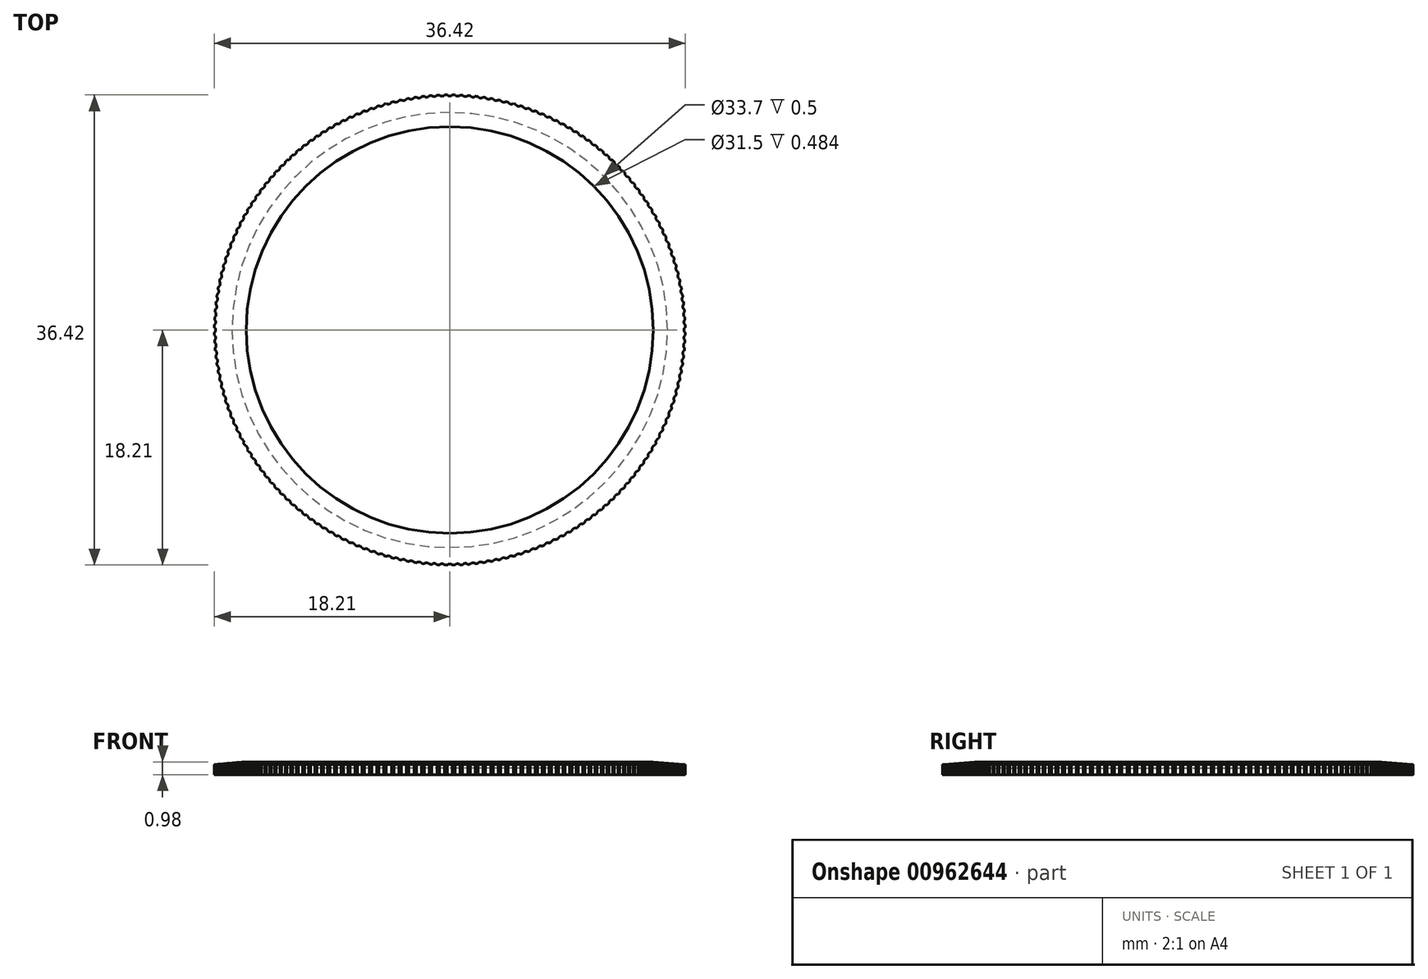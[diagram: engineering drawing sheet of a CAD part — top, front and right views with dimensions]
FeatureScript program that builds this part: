
annotation { "Feature Type Name" : "Feature", "Feature Type Description" : "" }
export const myFeature = defineFeature(function(context is Context, id is Id, definition is map)
    precondition{}
    {
        {
            assignVariable(context, id + "F0", {"name" : "dOut", "anyValue" : 36.43 * mm});
        }
        {
            assignVariable(context, id + "F1", {"name" : "dIn", "anyValue" : 31.5 * mm});
        }
        {
            assignVariable(context, id + "F2", {"name" : "bevelAngle", "anyValue" : 5 * degree});
        }
        {
            var Q0;
            Q0=qCreatedBy(makeId("Top.planeOp"),FACE);
            var sketch = newSketch(context, id + "F3", { "sketchPlane" : qUnion([Q0])});
            skCircle(sketch, "E0", {"center": v(0, 0) * mm, "radius": 18.21 * mm});
            skCircle(sketch, "E1", {"center": v(0, 0) * mm, "radius": 16.85 * mm});
            skCircle(sketch, "E2", {"center": v(0, 0) * mm, "radius": 15.75 * mm});
            skSolve(sketch);
        }
        {
            assignVariable(context, id + "F4", {"name" : "thickness", "anyValue" : 1.2 * mm});
        }
        {
            assignVariable(context, id + "F5", {"name" : "thickness_inside", "anyValue" : 0.7 * mm});
        }
        {
            var Q0;
            Q0=makeQuery(id+"F3.imprint","IMPRINT",FACE,{"disambiguationData":[TD([[makeQuery(id+"F3.imprint","IMPRINT",EDGE,{"derivedFrom":sQuery(id+"F3.wireOp",EDGE,"E0")}),1.0]])]});
            extrude(context, id + "F6", {"entities" : qUnion([Q0]), "oppositeDirection" : true, "depth" : getVariable(context, 'thickness'), "offsetDistance" : 25 * mm});
        }
        {
            var Q0;
            Q0=makeQuery(id+"F3.imprint","IMPRINT",FACE,{"disambiguationData":[TD([[makeQuery(id+"F3.imprint","IMPRINT",EDGE,{"derivedFrom":sQuery(id+"F3.wireOp",EDGE,"E1")}),1.0]])]});
            extrude(context, id + "F7", {"entities" : qUnion([Q0]), "operationType" : NewBodyOperationType.ADD, "oppositeDirection" : true, "depth" : getVariable(context, 'thickness_inside'), "offsetDistance" : 25 * mm});
        }
        {
            var Q0;
            Q0=makeQuery(id+"F6.opExtrude","CAP_EDGE",EDGE,{"disambiguationData":[OSD([sQuery(id+"F3.wireOp",EDGE,"E0")])],"isStart":true});
            chamfer(context, id + "F8", {"entities" : qUnion([Q0]), "chamferType" : ChamferType.OFFSET_ANGLE, "width" : getVariable(context, 'dOut') - getVariable(context, 'dIn'), "oppositeDirection" : false, "angle" : getVariable(context, 'bevelAngle'), "tangentPropagation" : true});
        }
        {
            var Q0;
            Q0=qCreatedBy(makeId("Top.planeOp"),FACE);
            var sketch = newSketch(context, id + "F9", { "sketchPlane" : qUnion([Q0])});
            skCircle(sketch, "E3.0", {"center": v(0, 0) * mm, "radius": 18.21 * mm, "construction": true});
            skCircle(sketch, "E4.0", {"center": v(0, 0) * mm, "radius": 16.85 * mm, "construction": true});
            skCircle(sketch, "E5", {"center": v(0, 18.36) * mm, "radius": 0.25 * mm});
            skCircle(sketch, "E6.1.0", {"center": v(-0.6, 18.36) * mm, "radius": 0.25 * mm});
            skCircle(sketch, "E6.2.0", {"center": v(-1.2, 18.33) * mm, "radius": 0.25 * mm});
            skCircle(sketch, "E6.3.0", {"center": v(-1.8, 18.28) * mm, "radius": 0.25 * mm});
            skCircle(sketch, "E6.4.0", {"center": v(-2.4, 18.2) * mm, "radius": 0.25 * mm});
            skCircle(sketch, "E6.5.0", {"center": v(-3, 18.12) * mm, "radius": 0.25 * mm});
            skCircle(sketch, "E6.6.0", {"center": v(-3.58, 18.01) * mm, "radius": 0.25 * mm});
            skCircle(sketch, "E6.7.0", {"center": v(-4.17, 17.89) * mm, "radius": 0.25 * mm});
            skCircle(sketch, "E6.8.0", {"center": v(-4.75, 17.74) * mm, "radius": 0.25 * mm});
            skCircle(sketch, "E6.9.0", {"center": v(-5.33, 17.57) * mm, "radius": 0.25 * mm});
            skCircle(sketch, "E6.10.0", {"center": v(-5.9, 17.4) * mm, "radius": 0.25 * mm});
            skCircle(sketch, "E6.11.0", {"center": v(-6.47, 17.19) * mm, "radius": 0.25 * mm});
            skCircle(sketch, "E6.12.0", {"center": v(-7.03, 16.97) * mm, "radius": 0.25 * mm});
            skCircle(sketch, "E6.13.0", {"center": v(-7.58, 16.73) * mm, "radius": 0.25 * mm});
            skCircle(sketch, "E6.14.0", {"center": v(-8.12, 16.47) * mm, "radius": 0.25 * mm});
            skCircle(sketch, "E6.15.0", {"center": v(-8.66, 16.2) * mm, "radius": 0.25 * mm});
            skCircle(sketch, "E6.16.0", {"center": v(-9.18, 15.9) * mm, "radius": 0.25 * mm});
            skCircle(sketch, "E6.17.0", {"center": v(-9.7, 15.6) * mm, "radius": 0.25 * mm});
            skCircle(sketch, "E6.18.0", {"center": v(-10.2, 15.27) * mm, "radius": 0.25 * mm});
            skCircle(sketch, "E6.19.0", {"center": v(-10.7, 14.93) * mm, "radius": 0.25 * mm});
            skCircle(sketch, "E6.20.0", {"center": v(-11.18, 14.57) * mm, "radius": 0.25 * mm});
            skCircle(sketch, "E6.21.0", {"center": v(-11.65, 14.2) * mm, "radius": 0.25 * mm});
            skCircle(sketch, "E6.22.0", {"center": v(-12.1, 13.8) * mm, "radius": 0.25 * mm});
            skCircle(sketch, "E6.23.0", {"center": v(-12.55, 13.4) * mm, "radius": 0.25 * mm});
            skCircle(sketch, "E7.1.24.0", {"center": v(-12.99, 12.99) * mm, "radius": 0.25 * mm});
            skCircle(sketch, "E7.1.25.0", {"center": v(-13.4, 12.55) * mm, "radius": 0.25 * mm});
            skCircle(sketch, "E7.1.26.0", {"center": v(-13.8, 12.1) * mm, "radius": 0.25 * mm});
            skCircle(sketch, "E7.1.27.0", {"center": v(-14.2, 11.65) * mm, "radius": 0.25 * mm});
            skCircle(sketch, "E7.1.28.0", {"center": v(-14.57, 11.18) * mm, "radius": 0.25 * mm});
            skCircle(sketch, "E7.1.29.0", {"center": v(-14.93, 10.7) * mm, "radius": 0.25 * mm});
            skCircle(sketch, "E7.1.30.0", {"center": v(-15.27, 10.2) * mm, "radius": 0.25 * mm});
            skCircle(sketch, "E7.1.31.0", {"center": v(-15.6, 9.7) * mm, "radius": 0.25 * mm});
            skCircle(sketch, "E7.1.32.0", {"center": v(-15.9, 9.18) * mm, "radius": 0.25 * mm});
            skCircle(sketch, "E7.1.33.0", {"center": v(-16.2, 8.66) * mm, "radius": 0.25 * mm});
            skCircle(sketch, "E7.1.34.0", {"center": v(-16.47, 8.12) * mm, "radius": 0.25 * mm});
            skCircle(sketch, "E7.1.35.0", {"center": v(-16.73, 7.58) * mm, "radius": 0.25 * mm});
            skCircle(sketch, "E7.1.36.0", {"center": v(-16.97, 7.03) * mm, "radius": 0.25 * mm});
            skCircle(sketch, "E7.1.37.0", {"center": v(-17.19, 6.47) * mm, "radius": 0.25 * mm});
            skCircle(sketch, "E7.1.38.0", {"center": v(-17.4, 5.9) * mm, "radius": 0.25 * mm});
            skCircle(sketch, "E7.1.39.0", {"center": v(-17.57, 5.33) * mm, "radius": 0.25 * mm});
            skCircle(sketch, "E7.1.40.0", {"center": v(-17.74, 4.75) * mm, "radius": 0.25 * mm});
            skCircle(sketch, "E7.1.41.0", {"center": v(-17.89, 4.17) * mm, "radius": 0.25 * mm});
            skCircle(sketch, "E7.1.42.0", {"center": v(-18.01, 3.58) * mm, "radius": 0.25 * mm});
            skCircle(sketch, "E7.1.43.0", {"center": v(-18.12, 3) * mm, "radius": 0.25 * mm});
            skCircle(sketch, "E7.1.44.0", {"center": v(-18.2, 2.4) * mm, "radius": 0.25 * mm});
            skCircle(sketch, "E7.1.45.0", {"center": v(-18.28, 1.8) * mm, "radius": 0.25 * mm});
            skCircle(sketch, "E7.1.46.0", {"center": v(-18.33, 1.2) * mm, "radius": 0.25 * mm});
            skCircle(sketch, "E7.1.47.0", {"center": v(-18.36, 0.6) * mm, "radius": 0.25 * mm});
            skCircle(sketch, "E7.1.48.0", {"center": v(-18.36, 0) * mm, "radius": 0.25 * mm});
            skCircle(sketch, "E7.1.49.0", {"center": v(-18.36, -0.6) * mm, "radius": 0.25 * mm});
            skCircle(sketch, "E7.1.50.0", {"center": v(-18.33, -1.2) * mm, "radius": 0.25 * mm});
            skCircle(sketch, "E7.1.51.0", {"center": v(-18.28, -1.8) * mm, "radius": 0.25 * mm});
            skCircle(sketch, "E7.1.52.0", {"center": v(-18.2, -2.4) * mm, "radius": 0.25 * mm});
            skCircle(sketch, "E7.1.53.0", {"center": v(-18.12, -3) * mm, "radius": 0.25 * mm});
            skCircle(sketch, "E7.1.54.0", {"center": v(-18.01, -3.58) * mm, "radius": 0.25 * mm});
            skCircle(sketch, "E7.1.55.0", {"center": v(-17.89, -4.17) * mm, "radius": 0.25 * mm});
            skCircle(sketch, "E7.1.56.0", {"center": v(-17.74, -4.75) * mm, "radius": 0.25 * mm});
            skCircle(sketch, "E7.1.57.0", {"center": v(-17.57, -5.33) * mm, "radius": 0.25 * mm});
            skCircle(sketch, "E7.1.58.0", {"center": v(-17.4, -5.9) * mm, "radius": 0.25 * mm});
            skCircle(sketch, "E7.1.59.0", {"center": v(-17.19, -6.47) * mm, "radius": 0.25 * mm});
            skCircle(sketch, "E7.1.60.0", {"center": v(-16.97, -7.03) * mm, "radius": 0.25 * mm});
            skCircle(sketch, "E7.1.61.0", {"center": v(-16.73, -7.58) * mm, "radius": 0.25 * mm});
            skCircle(sketch, "E7.1.62.0", {"center": v(-16.47, -8.12) * mm, "radius": 0.25 * mm});
            skCircle(sketch, "E7.1.63.0", {"center": v(-16.2, -8.66) * mm, "radius": 0.25 * mm});
            skCircle(sketch, "E7.1.64.0", {"center": v(-15.9, -9.18) * mm, "radius": 0.25 * mm});
            skCircle(sketch, "E7.1.65.0", {"center": v(-15.6, -9.7) * mm, "radius": 0.25 * mm});
            skCircle(sketch, "E7.1.66.0", {"center": v(-15.27, -10.2) * mm, "radius": 0.25 * mm});
            skCircle(sketch, "E7.1.67.0", {"center": v(-14.93, -10.7) * mm, "radius": 0.25 * mm});
            skCircle(sketch, "E7.1.68.0", {"center": v(-14.57, -11.18) * mm, "radius": 0.25 * mm});
            skCircle(sketch, "E7.1.69.0", {"center": v(-14.2, -11.65) * mm, "radius": 0.25 * mm});
            skCircle(sketch, "E7.1.70.0", {"center": v(-13.8, -12.1) * mm, "radius": 0.25 * mm});
            skCircle(sketch, "E7.1.71.0", {"center": v(-13.4, -12.55) * mm, "radius": 0.25 * mm});
            skCircle(sketch, "E7.1.72.0", {"center": v(-12.99, -12.99) * mm, "radius": 0.25 * mm});
            skCircle(sketch, "E7.1.73.0", {"center": v(-12.55, -13.4) * mm, "radius": 0.25 * mm});
            skCircle(sketch, "E7.1.74.0", {"center": v(-12.1, -13.8) * mm, "radius": 0.25 * mm});
            skCircle(sketch, "E7.1.75.0", {"center": v(-11.65, -14.2) * mm, "radius": 0.25 * mm});
            skCircle(sketch, "E7.1.76.0", {"center": v(-11.18, -14.57) * mm, "radius": 0.25 * mm});
            skCircle(sketch, "E7.1.77.0", {"center": v(-10.7, -14.93) * mm, "radius": 0.25 * mm});
            skCircle(sketch, "E7.1.78.0", {"center": v(-10.2, -15.27) * mm, "radius": 0.25 * mm});
            skCircle(sketch, "E7.1.79.0", {"center": v(-9.7, -15.6) * mm, "radius": 0.25 * mm});
            skCircle(sketch, "E7.1.80.0", {"center": v(-9.18, -15.9) * mm, "radius": 0.25 * mm});
            skCircle(sketch, "E7.1.81.0", {"center": v(-8.66, -16.2) * mm, "radius": 0.25 * mm});
            skCircle(sketch, "E7.1.82.0", {"center": v(-8.12, -16.47) * mm, "radius": 0.25 * mm});
            skCircle(sketch, "E7.1.83.0", {"center": v(-7.58, -16.73) * mm, "radius": 0.25 * mm});
            skCircle(sketch, "E7.1.84.0", {"center": v(-7.03, -16.97) * mm, "radius": 0.25 * mm});
            skCircle(sketch, "E7.1.85.0", {"center": v(-6.47, -17.19) * mm, "radius": 0.25 * mm});
            skCircle(sketch, "E7.1.86.0", {"center": v(-5.9, -17.4) * mm, "radius": 0.25 * mm});
            skCircle(sketch, "E7.1.87.0", {"center": v(-5.33, -17.57) * mm, "radius": 0.25 * mm});
            skCircle(sketch, "E7.1.88.0", {"center": v(-4.75, -17.74) * mm, "radius": 0.25 * mm});
            skCircle(sketch, "E7.1.89.0", {"center": v(-4.17, -17.89) * mm, "radius": 0.25 * mm});
            skCircle(sketch, "E7.1.90.0", {"center": v(-3.58, -18.01) * mm, "radius": 0.25 * mm});
            skCircle(sketch, "E7.1.91.0", {"center": v(-3, -18.12) * mm, "radius": 0.25 * mm});
            skCircle(sketch, "E7.1.92.0", {"center": v(-2.4, -18.2) * mm, "radius": 0.25 * mm});
            skCircle(sketch, "E7.1.93.0", {"center": v(-1.8, -18.28) * mm, "radius": 0.25 * mm});
            skCircle(sketch, "E7.1.94.0", {"center": v(-1.2, -18.33) * mm, "radius": 0.25 * mm});
            skCircle(sketch, "E7.1.95.0", {"center": v(-0.6, -18.36) * mm, "radius": 0.25 * mm});
            skCircle(sketch, "E7.1.96.0", {"center": v(0, -18.36) * mm, "radius": 0.25 * mm});
            skCircle(sketch, "E7.1.97.0", {"center": v(0.6, -18.36) * mm, "radius": 0.25 * mm});
            skCircle(sketch, "E7.1.98.0", {"center": v(1.2, -18.33) * mm, "radius": 0.25 * mm});
            skCircle(sketch, "E7.1.99.0", {"center": v(1.8, -18.28) * mm, "radius": 0.25 * mm});
            skCircle(sketch, "E7.1.100.0", {"center": v(2.4, -18.2) * mm, "radius": 0.25 * mm});
            skCircle(sketch, "E7.1.101.0", {"center": v(3, -18.12) * mm, "radius": 0.25 * mm});
            skCircle(sketch, "E7.1.102.0", {"center": v(3.58, -18.01) * mm, "radius": 0.25 * mm});
            skCircle(sketch, "E7.1.103.0", {"center": v(4.17, -17.89) * mm, "radius": 0.25 * mm});
            skCircle(sketch, "E7.1.104.0", {"center": v(4.75, -17.74) * mm, "radius": 0.25 * mm});
            skCircle(sketch, "E7.1.105.0", {"center": v(5.33, -17.57) * mm, "radius": 0.25 * mm});
            skCircle(sketch, "E7.1.106.0", {"center": v(5.9, -17.4) * mm, "radius": 0.25 * mm});
            skCircle(sketch, "E7.1.107.0", {"center": v(6.47, -17.19) * mm, "radius": 0.25 * mm});
            skCircle(sketch, "E7.1.108.0", {"center": v(7.03, -16.97) * mm, "radius": 0.25 * mm});
            skCircle(sketch, "E7.1.109.0", {"center": v(7.58, -16.73) * mm, "radius": 0.25 * mm});
            skCircle(sketch, "E7.1.110.0", {"center": v(8.12, -16.47) * mm, "radius": 0.25 * mm});
            skCircle(sketch, "E7.1.111.0", {"center": v(8.66, -16.2) * mm, "radius": 0.25 * mm});
            skCircle(sketch, "E7.1.112.0", {"center": v(9.18, -15.9) * mm, "radius": 0.25 * mm});
            skCircle(sketch, "E7.1.113.0", {"center": v(9.7, -15.6) * mm, "radius": 0.25 * mm});
            skCircle(sketch, "E7.1.114.0", {"center": v(10.2, -15.27) * mm, "radius": 0.25 * mm});
            skCircle(sketch, "E7.1.115.0", {"center": v(10.7, -14.93) * mm, "radius": 0.25 * mm});
            skCircle(sketch, "E7.1.116.0", {"center": v(11.18, -14.57) * mm, "radius": 0.25 * mm});
            skCircle(sketch, "E7.1.117.0", {"center": v(11.65, -14.2) * mm, "radius": 0.25 * mm});
            skCircle(sketch, "E7.1.118.0", {"center": v(12.1, -13.8) * mm, "radius": 0.25 * mm});
            skCircle(sketch, "E7.1.119.0", {"center": v(12.55, -13.4) * mm, "radius": 0.25 * mm});
            skCircle(sketch, "E7.1.120.0", {"center": v(12.99, -12.99) * mm, "radius": 0.25 * mm});
            skCircle(sketch, "E7.1.121.0", {"center": v(13.4, -12.55) * mm, "radius": 0.25 * mm});
            skCircle(sketch, "E7.1.122.0", {"center": v(13.8, -12.1) * mm, "radius": 0.25 * mm});
            skCircle(sketch, "E7.1.123.0", {"center": v(14.2, -11.65) * mm, "radius": 0.25 * mm});
            skCircle(sketch, "E7.1.124.0", {"center": v(14.57, -11.18) * mm, "radius": 0.25 * mm});
            skCircle(sketch, "E7.1.125.0", {"center": v(14.93, -10.7) * mm, "radius": 0.25 * mm});
            skCircle(sketch, "E7.1.126.0", {"center": v(15.27, -10.2) * mm, "radius": 0.25 * mm});
            skCircle(sketch, "E7.1.127.0", {"center": v(15.6, -9.7) * mm, "radius": 0.25 * mm});
            skCircle(sketch, "E7.1.128.0", {"center": v(15.9, -9.18) * mm, "radius": 0.25 * mm});
            skCircle(sketch, "E7.1.129.0", {"center": v(16.2, -8.66) * mm, "radius": 0.25 * mm});
            skCircle(sketch, "E7.1.130.0", {"center": v(16.47, -8.12) * mm, "radius": 0.25 * mm});
            skCircle(sketch, "E7.1.131.0", {"center": v(16.73, -7.58) * mm, "radius": 0.25 * mm});
            skCircle(sketch, "E7.1.132.0", {"center": v(16.97, -7.03) * mm, "radius": 0.25 * mm});
            skCircle(sketch, "E7.1.133.0", {"center": v(17.19, -6.47) * mm, "radius": 0.25 * mm});
            skCircle(sketch, "E7.1.134.0", {"center": v(17.4, -5.9) * mm, "radius": 0.25 * mm});
            skCircle(sketch, "E7.1.135.0", {"center": v(17.57, -5.33) * mm, "radius": 0.25 * mm});
            skCircle(sketch, "E7.1.136.0", {"center": v(17.74, -4.75) * mm, "radius": 0.25 * mm});
            skCircle(sketch, "E7.1.137.0", {"center": v(17.89, -4.17) * mm, "radius": 0.25 * mm});
            skCircle(sketch, "E7.1.138.0", {"center": v(18.01, -3.58) * mm, "radius": 0.25 * mm});
            skCircle(sketch, "E7.1.139.0", {"center": v(18.12, -3) * mm, "radius": 0.25 * mm});
            skCircle(sketch, "E7.1.140.0", {"center": v(18.2, -2.4) * mm, "radius": 0.25 * mm});
            skCircle(sketch, "E7.1.141.0", {"center": v(18.28, -1.8) * mm, "radius": 0.25 * mm});
            skCircle(sketch, "E7.1.142.0", {"center": v(18.33, -1.2) * mm, "radius": 0.25 * mm});
            skCircle(sketch, "E7.1.143.0", {"center": v(18.36, -0.6) * mm, "radius": 0.25 * mm});
            skCircle(sketch, "E7.1.144.0", {"center": v(18.36, 0) * mm, "radius": 0.25 * mm});
            skCircle(sketch, "E7.1.145.0", {"center": v(18.36, 0.6) * mm, "radius": 0.25 * mm});
            skCircle(sketch, "E7.1.146.0", {"center": v(18.33, 1.2) * mm, "radius": 0.25 * mm});
            skCircle(sketch, "E7.1.147.0", {"center": v(18.28, 1.8) * mm, "radius": 0.25 * mm});
            skCircle(sketch, "E7.1.148.0", {"center": v(18.2, 2.4) * mm, "radius": 0.25 * mm});
            skCircle(sketch, "E7.1.149.0", {"center": v(18.12, 3) * mm, "radius": 0.25 * mm});
            skCircle(sketch, "E7.1.150.0", {"center": v(18.01, 3.58) * mm, "radius": 0.25 * mm});
            skCircle(sketch, "E7.1.151.0", {"center": v(17.89, 4.17) * mm, "radius": 0.25 * mm});
            skCircle(sketch, "E7.1.152.0", {"center": v(17.74, 4.75) * mm, "radius": 0.25 * mm});
            skCircle(sketch, "E7.1.153.0", {"center": v(17.57, 5.33) * mm, "radius": 0.25 * mm});
            skCircle(sketch, "E7.1.154.0", {"center": v(17.4, 5.9) * mm, "radius": 0.25 * mm});
            skCircle(sketch, "E7.1.155.0", {"center": v(17.19, 6.47) * mm, "radius": 0.25 * mm});
            skCircle(sketch, "E7.1.156.0", {"center": v(16.97, 7.03) * mm, "radius": 0.25 * mm});
            skCircle(sketch, "E7.1.157.0", {"center": v(16.73, 7.58) * mm, "radius": 0.25 * mm});
            skCircle(sketch, "E7.1.158.0", {"center": v(16.47, 8.12) * mm, "radius": 0.25 * mm});
            skCircle(sketch, "E7.1.159.0", {"center": v(16.2, 8.66) * mm, "radius": 0.25 * mm});
            skCircle(sketch, "E7.1.160.0", {"center": v(15.9, 9.18) * mm, "radius": 0.25 * mm});
            skCircle(sketch, "E7.1.161.0", {"center": v(15.6, 9.7) * mm, "radius": 0.25 * mm});
            skCircle(sketch, "E7.1.162.0", {"center": v(15.27, 10.2) * mm, "radius": 0.25 * mm});
            skCircle(sketch, "E7.1.163.0", {"center": v(14.93, 10.7) * mm, "radius": 0.25 * mm});
            skCircle(sketch, "E7.1.164.0", {"center": v(14.57, 11.18) * mm, "radius": 0.25 * mm});
            skCircle(sketch, "E7.1.165.0", {"center": v(14.2, 11.65) * mm, "radius": 0.25 * mm});
            skCircle(sketch, "E7.1.166.0", {"center": v(13.8, 12.1) * mm, "radius": 0.25 * mm});
            skCircle(sketch, "E7.1.167.0", {"center": v(13.4, 12.55) * mm, "radius": 0.25 * mm});
            skCircle(sketch, "E7.1.168.0", {"center": v(12.99, 12.99) * mm, "radius": 0.25 * mm});
            skCircle(sketch, "E7.1.169.0", {"center": v(12.55, 13.4) * mm, "radius": 0.25 * mm});
            skCircle(sketch, "E7.1.170.0", {"center": v(12.1, 13.8) * mm, "radius": 0.25 * mm});
            skCircle(sketch, "E7.1.171.0", {"center": v(11.65, 14.2) * mm, "radius": 0.25 * mm});
            skCircle(sketch, "E7.1.172.0", {"center": v(11.18, 14.57) * mm, "radius": 0.25 * mm});
            skCircle(sketch, "E7.1.173.0", {"center": v(10.7, 14.93) * mm, "radius": 0.25 * mm});
            skCircle(sketch, "E7.1.174.0", {"center": v(10.2, 15.27) * mm, "radius": 0.25 * mm});
            skCircle(sketch, "E7.1.175.0", {"center": v(9.7, 15.6) * mm, "radius": 0.25 * mm});
            skCircle(sketch, "E7.1.176.0", {"center": v(9.18, 15.9) * mm, "radius": 0.25 * mm});
            skCircle(sketch, "E7.1.177.0", {"center": v(8.66, 16.2) * mm, "radius": 0.25 * mm});
            skCircle(sketch, "E7.1.178.0", {"center": v(8.12, 16.47) * mm, "radius": 0.25 * mm});
            skCircle(sketch, "E7.1.179.0", {"center": v(7.58, 16.73) * mm, "radius": 0.25 * mm});
            skCircle(sketch, "E7.1.180.0", {"center": v(7.03, 16.97) * mm, "radius": 0.25 * mm});
            skCircle(sketch, "E7.1.181.0", {"center": v(6.47, 17.19) * mm, "radius": 0.25 * mm});
            skCircle(sketch, "E7.1.182.0", {"center": v(5.9, 17.4) * mm, "radius": 0.25 * mm});
            skCircle(sketch, "E7.1.183.0", {"center": v(5.33, 17.57) * mm, "radius": 0.25 * mm});
            skCircle(sketch, "E7.1.184.0", {"center": v(4.75, 17.74) * mm, "radius": 0.25 * mm});
            skCircle(sketch, "E7.1.185.0", {"center": v(4.17, 17.89) * mm, "radius": 0.25 * mm});
            skCircle(sketch, "E7.1.186.0", {"center": v(3.58, 18.01) * mm, "radius": 0.25 * mm});
            skCircle(sketch, "E7.1.187.0", {"center": v(3, 18.12) * mm, "radius": 0.25 * mm});
            skCircle(sketch, "E7.1.188.0", {"center": v(2.4, 18.2) * mm, "radius": 0.25 * mm});
            skCircle(sketch, "E7.1.189.0", {"center": v(1.8, 18.28) * mm, "radius": 0.25 * mm});
            skCircle(sketch, "E7.1.190.0", {"center": v(1.2, 18.33) * mm, "radius": 0.25 * mm});
            skCircle(sketch, "E7.1.191.0", {"center": v(0.6, 18.36) * mm, "radius": 0.25 * mm});
            skSolve(sketch);
        }
        {
            var Q0;
            Q0 = qSketchRegion(id + "F9", true);
            extrude(context, id + "F10", {"entities" : qUnion([Q0]), "operationType" : NewBodyOperationType.REMOVE, "oppositeDirection" : true, "depth" : getVariable(context, 'thickness'), "offsetDistance" : 25 * mm});
        }
    });
